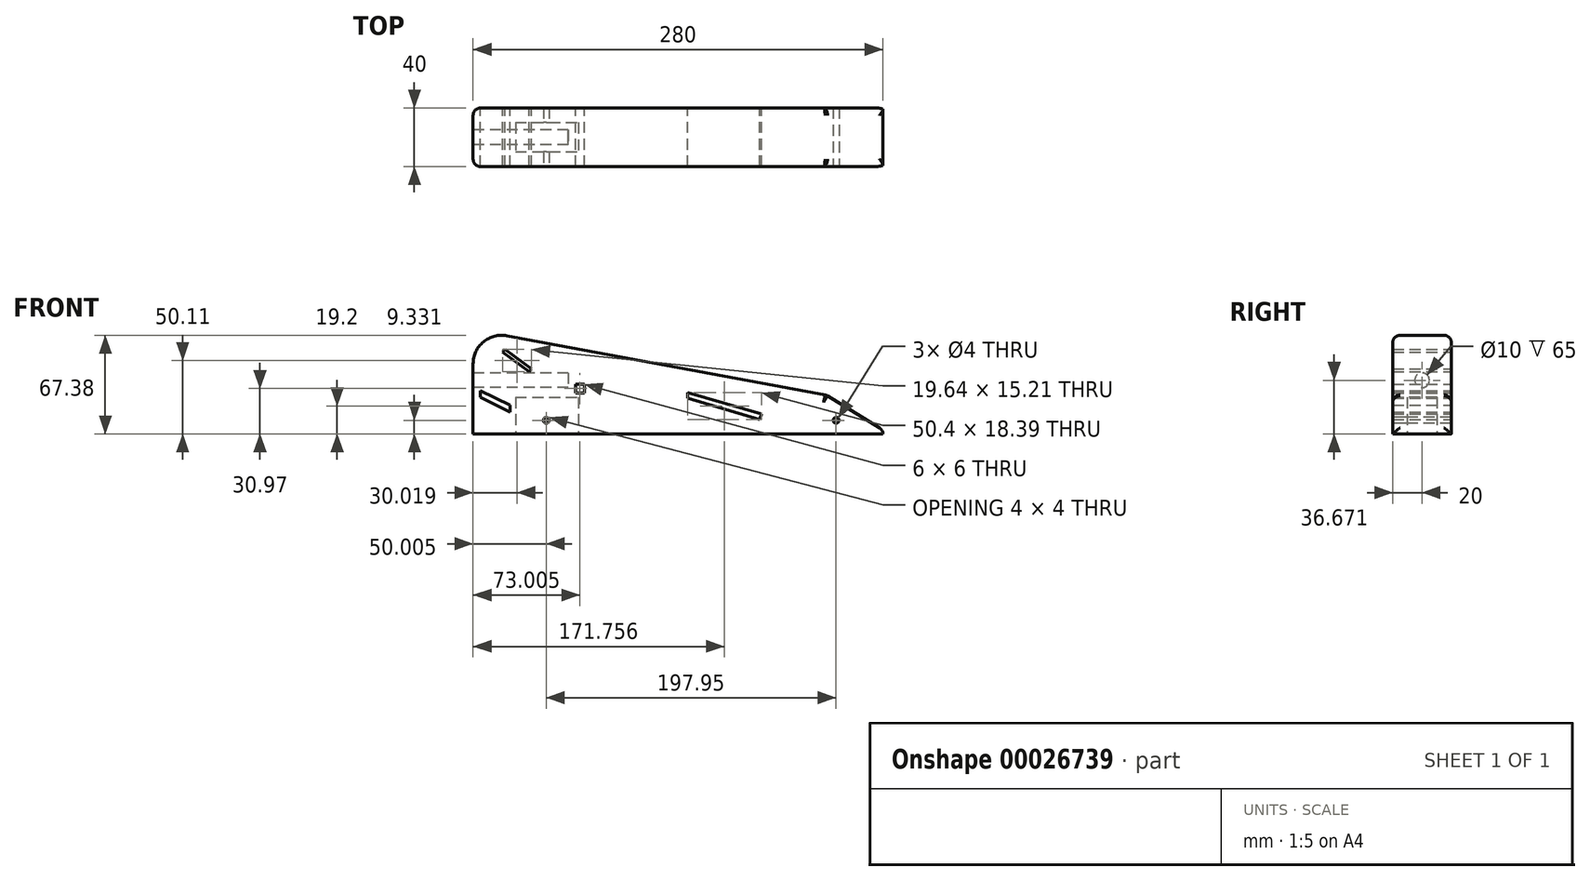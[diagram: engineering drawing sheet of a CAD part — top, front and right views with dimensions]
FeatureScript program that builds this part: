
annotation { "Feature Type Name" : "Feature", "Feature Type Description" : "" }
export const myFeature = defineFeature(function(context is Context, id is Id, definition is map)
    precondition{}
    {
        {
            var Q0;
            Q0=qCreatedBy(makeId("Front.planeOp"),FACE);
            var sketch = newSketch(context, id + "F0", { "sketchPlane" : qUnion([Q0])});
            skLineSegment(sketch, "E0.bottom", {"start": v(-73.62, -33.97) * mm, "end": v(206.38, -33.97) * mm});
            skLineSegment(sketch, "E0.top", {"start": v(-73.62, 37.36) * mm, "end": v(206.38, 37.36) * mm});
            skLineSegment(sketch, "E0.left", {"start": v(-73.62, -33.97) * mm, "end": v(-73.62, 13.94) * mm});
            skLineSegment(sketch, "E0.right", {"start": v(206.38, -33.97) * mm, "end": v(206.38, -31.3) * mm});
            skLineSegment(sketch, "E1", {"start": v(-50.6, 33.08) * mm, "end": v(190.04, -11.63) * mm});
            skPoint(sketch, "E2.newPointB", {"position": v(206.38, 36.03) * mm});
            skArc(sketch, "E2.filletArc", {"start": v(206.38, -31.3) * mm, "mid": v(201.76, -18.5) * mm, "end": v(190.04, -11.63) * mm});
            skPoint(sketch, "E3.visualSharp", {"position": v(-73.62, 37.36) * mm});
            skArc(sketch, "E3.filletArc", {"start": v(-50.6, 33.08) * mm, "mid": v(-66.6, 28.91) * mm, "end": v(-73.62, 13.94) * mm});
            skLineSegment(sketch, "E4.bottom", {"start": v(2.38, 0) * mm, "end": v(-3.62, 0) * mm});
            skLineSegment(sketch, "E4.top", {"start": v(2.38, -6) * mm, "end": v(-3.62, -6) * mm});
            skLineSegment(sketch, "E4.left", {"start": v(2.38, 0) * mm, "end": v(2.38, -6) * mm});
            skLineSegment(sketch, "E4.right", {"start": v(-3.62, 0) * mm, "end": v(-3.62, -6) * mm});
            skLineSegment(sketch, "E5", {"start": v(-68.62, -9.03) * mm, "end": v(-48.43, -18.97) * mm});
            skLineSegment(sketch, "E6", {"start": v(-48.43, -18.97) * mm, "end": v(-48.43, -14.36) * mm});
            skLineSegment(sketch, "E7", {"start": v(-48.43, -14.36) * mm, "end": v(-68.62, -4.42) * mm});
            skLineSegment(sketch, "E8", {"start": v(-68.62, -4.42) * mm, "end": v(-68.62, -9.03) * mm});
            skLineSegment(sketch, "E9", {"start": v(-53.42, 21.8) * mm, "end": v(-35.25, 8.53) * mm});
            skLineSegment(sketch, "E10", {"start": v(-35.25, 8.53) * mm, "end": v(-33.78, 10.55) * mm});
            skLineSegment(sketch, "E11", {"start": v(-33.78, 10.55) * mm, "end": v(-51.85, 23.75) * mm});
            skLineSegment(sketch, "E12", {"start": v(-51.85, 23.75) * mm, "end": v(-53.42, 21.8) * mm});
            skLineSegment(sketch, "E13", {"start": v(72.94, -5.57) * mm, "end": v(123.33, -20.28) * mm});
            skLineSegment(sketch, "E14", {"start": v(123.33, -20.28) * mm, "end": v(122.26, -23.97) * mm});
            skLineSegment(sketch, "E15", {"start": v(122.26, -23.97) * mm, "end": v(72.94, -9.57) * mm});
            skLineSegment(sketch, "E16", {"start": v(72.94, -9.57) * mm, "end": v(72.94, -5.57) * mm});
            skLineSegment(sketch, "E17", {"start": v(206.38, -31.3) * mm, "end": v(167.69, -7.48) * mm});
            skSolve(sketch);
        }
        {
            var Q0;
            Q0=makeQuery(id+"F0.imprint","IMPRINT",FACE,{"disambiguationData":[TD([[makeQuery(id+"F0.imprint","IMPRINT",EDGE,{"derivedFrom":sQuery(id+"F0.wireOp",EDGE,"E0.bottom")}),1.0]])]});
            extrude(context, id + "F1", {"entities" : qUnion([Q0]), "depth" : 40 * mm});
        }
        {
            var Q0;
            Q0=makeQuery(id+"F1.opExtrude","SWEPT_FACE",FACE,{"disambiguationData":[OSD([sQuery(id+"F0.wireOp",EDGE,"E0.left")])]});
            var sketch = newSketch(context, id + "F2", { "sketchPlane" : qUnion([Q0])});
            skCircle(sketch, "E18", {"center": v(20, 2.7) * mm, "radius": 5 * mm});
            skSolve(sketch);
        }
        {
            var Q0;
            Q0=makeQuery(id+"F2.imprint","IMPRINT",FACE,{"disambiguationData":[TD([[makeQuery(id+"F2.imprint","IMPRINT",EDGE,{"derivedFrom":sQuery(id+"F2.wireOp",EDGE,"E18")}),1.0]])]});
            extrude(context, id + "F3", {"entities" : qUnion([Q0]), "operationType" : NewBodyOperationType.REMOVE, "oppositeDirection" : true, "depth" : 65 * mm});
        }
        {
            var Q0;
            Q0=makeQuery(id+"F1.opExtrude","CAP_FACE",FACE,{"disambiguationData":[OSD([sQuery(id+"F0.wireOp",EDGE,"E0.bottom"),sQuery(id+"F0.wireOp",EDGE,"E0.top"),sQuery(id+"F0.wireOp",EDGE,"E0.left"),sQuery(id+"F0.wireOp",EDGE,"E0.right")])],"isStart":false});
            var sketch = newSketch(context, id + "F4", { "sketchPlane" : qUnion([Q0])});
            skCircle(sketch, "E19", {"center": v(-23.62, -24.64) * mm, "radius": 2 * mm});
            skCircle(sketch, "E20", {"center": v(174.33, -24.64) * mm, "radius": 2 * mm});
            skSolve(sketch);
        }
        {
            var Q0;
            Q0=makeQuery(id+"F4.imprint","IMPRINT",FACE,{"disambiguationData":[TD([[makeQuery(id+"F4.imprint","IMPRINT",EDGE,{"derivedFrom":sQuery(id+"F4.wireOp",EDGE,"E19")}),1.0]])]});
            var Q1;
            Q1=makeQuery(id+"F4.imprint","IMPRINT",FACE,{"disambiguationData":[TD([[makeQuery(id+"F4.imprint","IMPRINT",EDGE,{"derivedFrom":sQuery(id+"F4.wireOp",EDGE,"E20")}),1.0]])]});
            extrude(context, id + "F5", {"entities" : qUnion([Q0, Q1]), "operationType" : NewBodyOperationType.REMOVE, "endBound" : BoundingType.THROUGH_ALL, "oppositeDirection" : true, "depth" : 25 * mm});
        }
        {
            var Q0;
            Q0=makeQuery(id+"F1.opExtrude","SWEPT_FACE",FACE,{"disambiguationData":[OSD([sQuery(id+"F0.wireOp",EDGE,"E0.bottom")])]});
            var sketch = newSketch(context, id + "F6", { "sketchPlane" : qUnion([Q0])});
            skLineSegment(sketch, "E21.bottom", {"start": v(-44.62, 10) * mm, "end": v(-1.62, 10) * mm});
            skLineSegment(sketch, "E21.top", {"start": v(-44.62, 30) * mm, "end": v(-1.62, 30) * mm});
            skLineSegment(sketch, "E21.left", {"start": v(-44.62, 10) * mm, "end": v(-44.62, 30) * mm});
            skLineSegment(sketch, "E21.right", {"start": v(-1.62, 10) * mm, "end": v(-1.62, 30) * mm});
            skSolve(sketch);
        }
        {
            var Q0;
            Q0=makeQuery(id+"F6.imprint","IMPRINT",FACE,{"disambiguationData":[TD([[makeQuery(id+"F6.imprint","IMPRINT",EDGE,{"derivedFrom":sQuery(id+"F6.wireOp",EDGE,"E21.bottom")}),1.0]])]});
            extrude(context, id + "F7", {"entities" : qUnion([Q0]), "operationType" : NewBodyOperationType.REMOVE, "oppositeDirection" : true, "depth" : 25 * mm});
        }
        {
            var Q0;
            Q0=makeQuery(id+"F1.opExtrude","SWEPT_FACE",FACE,{"disambiguationData":[OSD([sQuery(id+"F0.wireOp",EDGE,"E1")])]});
            fillet(context, id + "F8", {"entities" : qUnion([Q0]), "radius" : 5 * mm, "tangentPropagation" : true, "allowEdgeOverflow" : false});
        }
        {
            var Q0;
            Q0=makeQuery(id+"F1.opExtrude","CAP_EDGE",EDGE,{"disambiguationData":[OSD([sQuery(id+"F0.wireOp",EDGE,"E17")])],"isStart":true});
            var Q1;
            Q1=makeQuery(id+"F1.opExtrude","SWEPT_EDGE",EDGE,{"disambiguationData":[OSD([sQuery(id+"F0.wireOp",EDGE,"E0.right"),sQuery(id+"F0.wireOp",EDGE,"E2.filletArc"),sQuery(id+"F0.wireOp",EDGE,"E17")])]});
            var Q2;
            Q2=makeQuery(id+"F1.opExtrude","CAP_EDGE",EDGE,{"disambiguationData":[OSD([sQuery(id+"F0.wireOp",EDGE,"E17")])],"isStart":false});
            fillet(context, id + "F9", {"entities" : qUnion([Q0, Q1, Q2]), "radius" : 5 * mm, "tangentPropagation" : true, "allowEdgeOverflow" : false});
        }
    });
